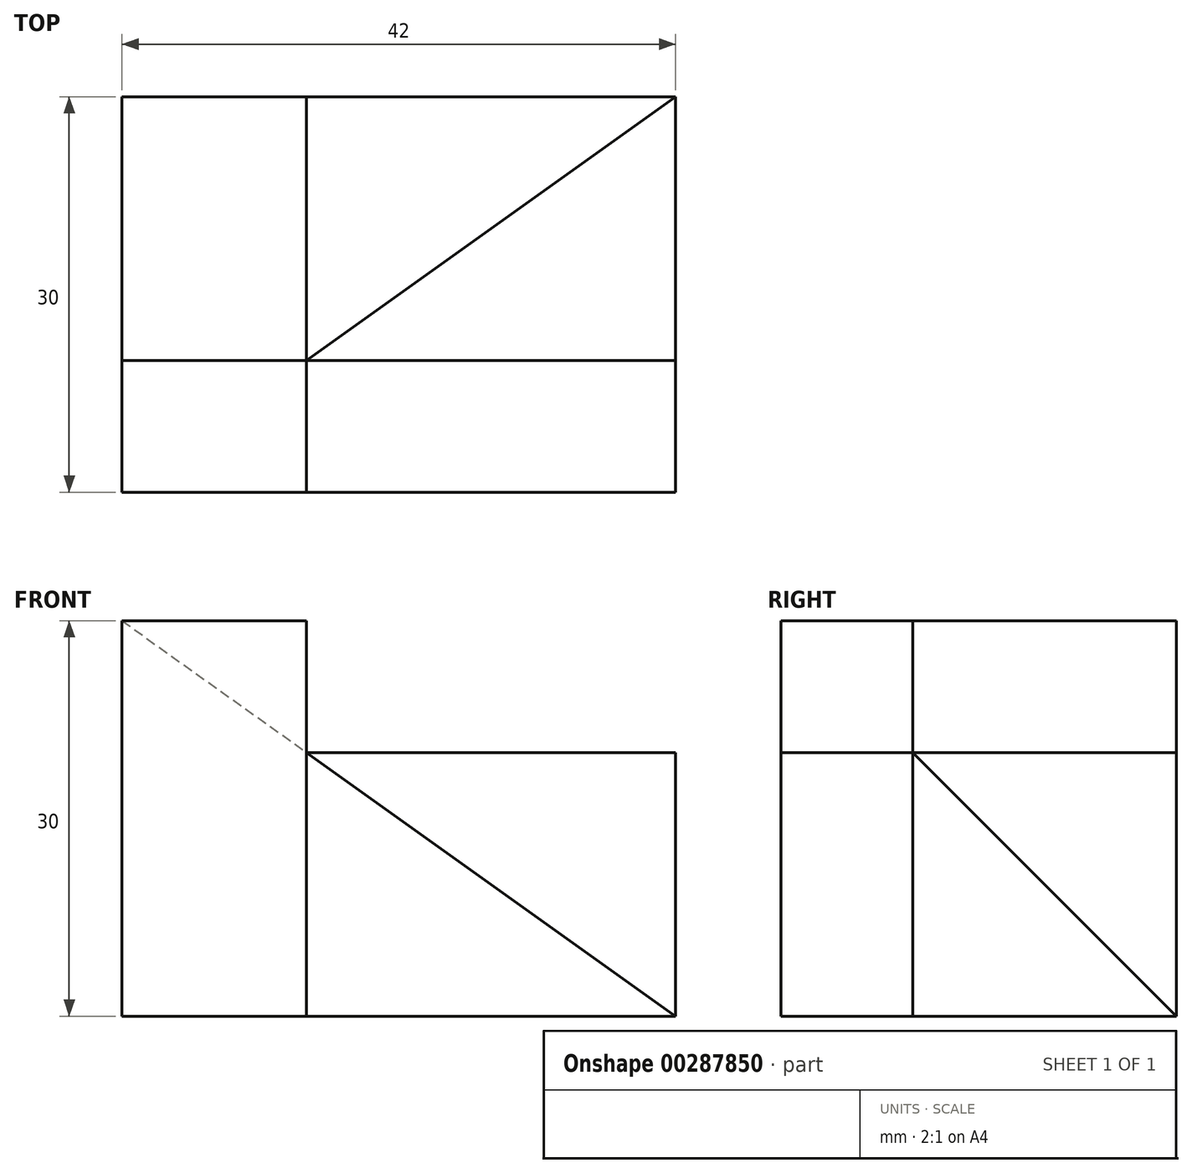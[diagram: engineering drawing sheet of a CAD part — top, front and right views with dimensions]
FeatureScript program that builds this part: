
annotation { "Feature Type Name" : "Feature", "Feature Type Description" : "" }
export const myFeature = defineFeature(function(context is Context, id is Id, definition is map)
    precondition{}
    {
        {
            var Q0;
            Q0=qCreatedBy(makeId("Front.planeOp"),FACE);
            var sketch = newSketch(context, id + "F0", { "sketchPlane" : qUnion([Q0])});
            skLineSegment(sketch, "E0.bottom", {"start": v(0, 0) * mm, "end": v(42, 0) * mm});
            skLineSegment(sketch, "E0.top", {"start": v(0, 30) * mm, "end": v(42, 30) * mm});
            skLineSegment(sketch, "E0.left", {"start": v(0, 0) * mm, "end": v(0, 30) * mm});
            skLineSegment(sketch, "E0.right", {"start": v(42, 0) * mm, "end": v(42, 30) * mm});
            skLineSegment(sketch, "E1.bottom", {"start": v(42, 30) * mm, "end": v(14, 30) * mm});
            skLineSegment(sketch, "E1.top", {"start": v(42, 20) * mm, "end": v(14, 20) * mm});
            skLineSegment(sketch, "E1.left", {"start": v(42, 30) * mm, "end": v(42, 20) * mm});
            skLineSegment(sketch, "E1.right", {"start": v(14, 30) * mm, "end": v(14, 20) * mm});
            skSolve(sketch);
        }
        {
            var Q0;
            Q0=makeQuery(id+"F0.imprint","IMPRINT",FACE,{"disambiguationData":[TD([[makeQuery(id+"F0.imprint","IMPRINT",EDGE,{"derivedFrom":sQuery(id+"F0.wireOp",EDGE,"E0.bottom")}),1.0]])]});
            extrude(context, id + "F1", {"entities" : qUnion([Q0]), "depth" : 30 * mm});
        }
        {
            var Q0;
            Q0=makeQuery(id+"F1.opExtrude","CAP_FACE",FACE,{"disambiguationData":[OSD([sQuery(id+"F0.wireOp",EDGE,"E0.bottom"),sQuery(id+"F0.wireOp",EDGE,"E0.top"),sQuery(id+"F0.wireOp",EDGE,"E0.left"),sQuery(id+"F0.wireOp",EDGE,"E0.right"),sQuery(id+"F0.wireOp",EDGE,"E1.top"),sQuery(id+"F0.wireOp",EDGE,"E1.right")])],"isStart":true});
            var sketch = newSketch(context, id + "F2", { "sketchPlane" : qUnion([Q0])});
            skLineSegment(sketch, "E2", {"start": v(0, 30) * mm, "end": v(-14, 20) * mm});
            skSolve(sketch);
        }
        {
            var Q0;
            Q0=makeQuery(id+"F2.imprint","IMPRINT",FACE,{"disambiguationData":[TD([[makeQuery(id+"F2.imprint","IMPRINT",EDGE,{"derivedFrom":sQuery(id+"F2.wireOp",EDGE,"E2")}),-1.0]])]});
            extrude(context, id + "F3", {"entities" : qUnion([Q0]), "operationType" : NewBodyOperationType.REMOVE, "flatOperationType" : FlatOperationType.REMOVE, "oppositeDirection" : true, "offsetDistance" : 25 * mm, "depth" : 20 * mm, "domain" : OperationDomain.MODEL});
        }
        {
            var Q0;
            Q0=makeQuery(id+"F1.opExtrude","CAP_FACE",FACE,{"disambiguationData":[OSD([sQuery(id+"F0.wireOp",EDGE,"E0.bottom"),sQuery(id+"F0.wireOp",EDGE,"E0.top"),sQuery(id+"F0.wireOp",EDGE,"E0.left"),sQuery(id+"F0.wireOp",EDGE,"E0.right"),sQuery(id+"F0.wireOp",EDGE,"E1.top"),sQuery(id+"F0.wireOp",EDGE,"E1.right")])],"isStart":false});
            var sketch = newSketch(context, id + "F4", { "sketchPlane" : qUnion([Q0])});
            skLineSegment(sketch, "E3", {"start": v(14, 20) * mm, "end": v(42, 0) * mm});
            skLineSegment(sketch, "E4", {"start": v(14, 20) * mm, "end": v(14, 0) * mm});
            skSolve(sketch);
        }
        {
            var Q0;
            Q0=makeQuery(id+"F4.imprint","IMPRINT",FACE,{"disambiguationData":[TD([[makeQuery(id+"F4.imprint","IMPRINT",EDGE,{"derivedFrom":sQuery(id+"F4.wireOp",EDGE,"E3")}),1.0]])]});
            extrude(context, id + "F5", {"entities" : qUnion([Q0]), "operationType" : NewBodyOperationType.REMOVE, "flatOperationType" : FlatOperationType.REMOVE, "endBound" : BoundingType.THROUGH_ALL, "oppositeDirection" : true, "offsetDistance" : 25 * mm, "depth" : 10 * mm, "domain" : OperationDomain.MODEL});
        }
        {
            var Q0;
            Q0=makeQuery(id+"F1.opExtrude","SWEPT_FACE",FACE,{"disambiguationData":[OSD([sQuery(id+"F0.wireOp",EDGE,"E0.bottom")])]});
            var sketch = newSketch(context, id + "F6", { "sketchPlane" : qUnion([Q0])});
            skLineSegment(sketch, "E5.bottom", {"start": v(42, 0) * mm, "end": v(14, 0) * mm});
            skLineSegment(sketch, "E5.top", {"start": v(42, 20) * mm, "end": v(14, 20) * mm});
            skLineSegment(sketch, "E5.left", {"start": v(42, 0) * mm, "end": v(42, 20) * mm});
            skLineSegment(sketch, "E5.right", {"start": v(14, 0) * mm, "end": v(14, 20) * mm});
            skLineSegment(sketch, "E6", {"start": v(42, 0) * mm, "end": v(14, 20) * mm});
            skSolve(sketch);
        }
        {
            var Q0;
            Q0=makeQuery(id+"F6.imprint","IMPRINT",FACE,{"disambiguationData":[TD([[makeQuery(id+"F6.imprint","IMPRINT",EDGE,{"derivedFrom":sQuery(id+"F6.wireOp",EDGE,"E5.bottom")}),1.0]])]});
            extrude(context, id + "F7", {"entities" : qUnion([Q0]), "operationType" : NewBodyOperationType.ADD, "oppositeDirection" : true, "depth" : 20 * mm});
        }
        {
            var Q0;
            Q0=makeQuery(id+"F4.imprint","IMPRINT",FACE,{"disambiguationData":[TD([[makeQuery(id+"F4.imprint","IMPRINT",EDGE,{"derivedFrom":sQuery(id+"F4.wireOp",EDGE,"E3")}),1.0]])]});
            extrude(context, id + "F8", {"entities" : qUnion([Q0]), "operationType" : NewBodyOperationType.ADD, "oppositeDirection" : true, "depth" : 10 * mm});
        }
        {
            var Q0;
            {var subQ0=sQuery(id+"F4.wireOp",EDGE,"E3");Q0=makeQuery(id+"F4.imprint","IMPRINT",FACE,{"disambiguationData":[TD([[makeQuery(id+"F4.imprint","IMPRINT",EDGE,{"derivedFrom":subQ0}),-1.0]])]});}
            extrude(context, id + "F9", {"entities" : qUnion([Q0]), "operationType" : NewBodyOperationType.REMOVE, "oppositeDirection" : true, "depth" : 10 * mm});
        }
    });
